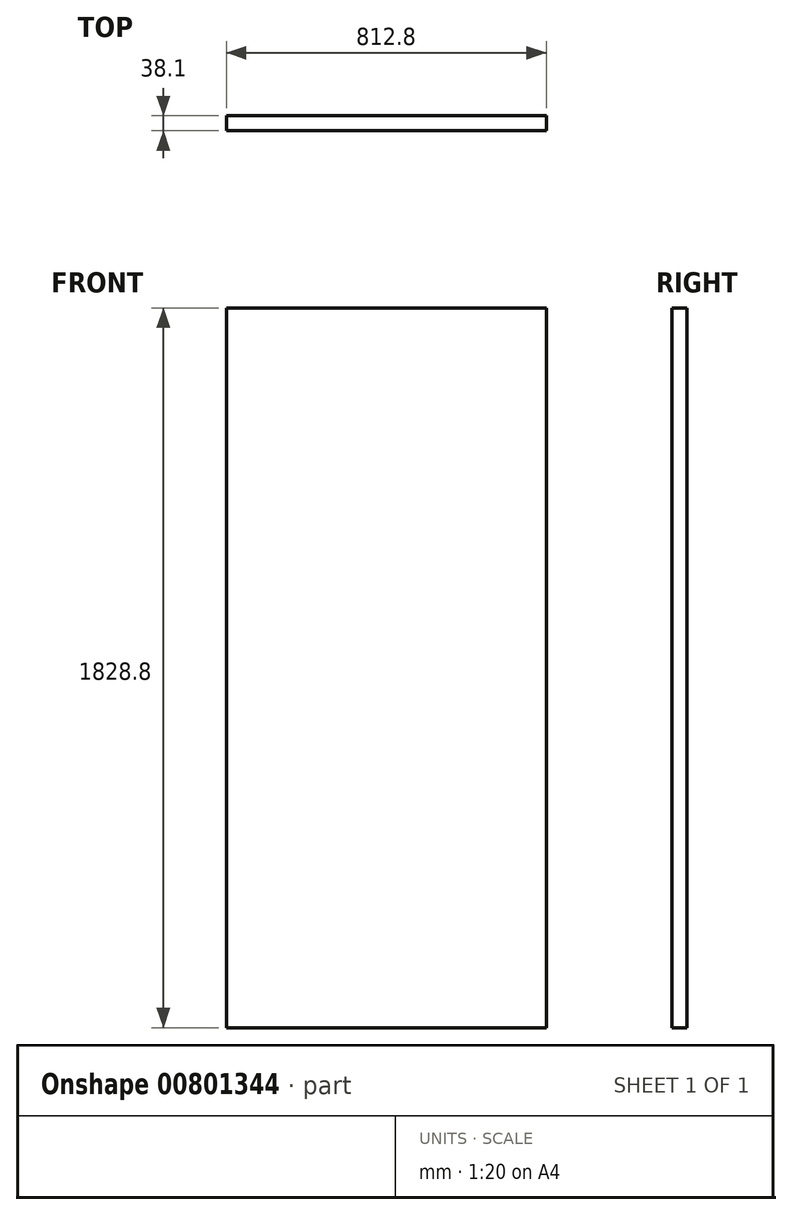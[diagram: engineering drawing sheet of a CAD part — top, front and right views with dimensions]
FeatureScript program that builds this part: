
annotation { "Feature Type Name" : "Feature", "Feature Type Description" : "" }
export const myFeature = defineFeature(function(context is Context, id is Id, definition is map)
    precondition{}
    {
        {
            var Q0;
            Q0=qCreatedBy(makeId("Front.planeOp"),FACE);
            var sketch = newSketch(context, id + "F0", { "sketchPlane" : qUnion([Q0])});
            skLineSegment(sketch, "E0.bottom", {"start": v(0, 0) * mm, "end": v(-812.8, 0) * mm});
            skLineSegment(sketch, "E0.top", {"start": v(0, 1828.8) * mm, "end": v(-812.8, 1828.8) * mm});
            skLineSegment(sketch, "E0.left", {"start": v(0, 0) * mm, "end": v(0, 1828.8) * mm});
            skLineSegment(sketch, "E0.right", {"start": v(-812.8, 0) * mm, "end": v(-812.8, 1828.8) * mm});
            skSolve(sketch);
        }
        {
            var Q0;
            Q0=makeQuery(id+"F0.imprint","IMPRINT",FACE,{"disambiguationData":[TD([[makeQuery(id+"F0.imprint","IMPRINT",EDGE,{"derivedFrom":sQuery(id+"F0.wireOp",EDGE,"E0.bottom")}),-1.0]])]});
            extrude(context, id + "F1", {"entities" : qUnion([Q0]), "oppositeDirection" : true, "depth" : 38.1 * mm, "offsetDistance" : 25.4 * mm});
        }
    });
